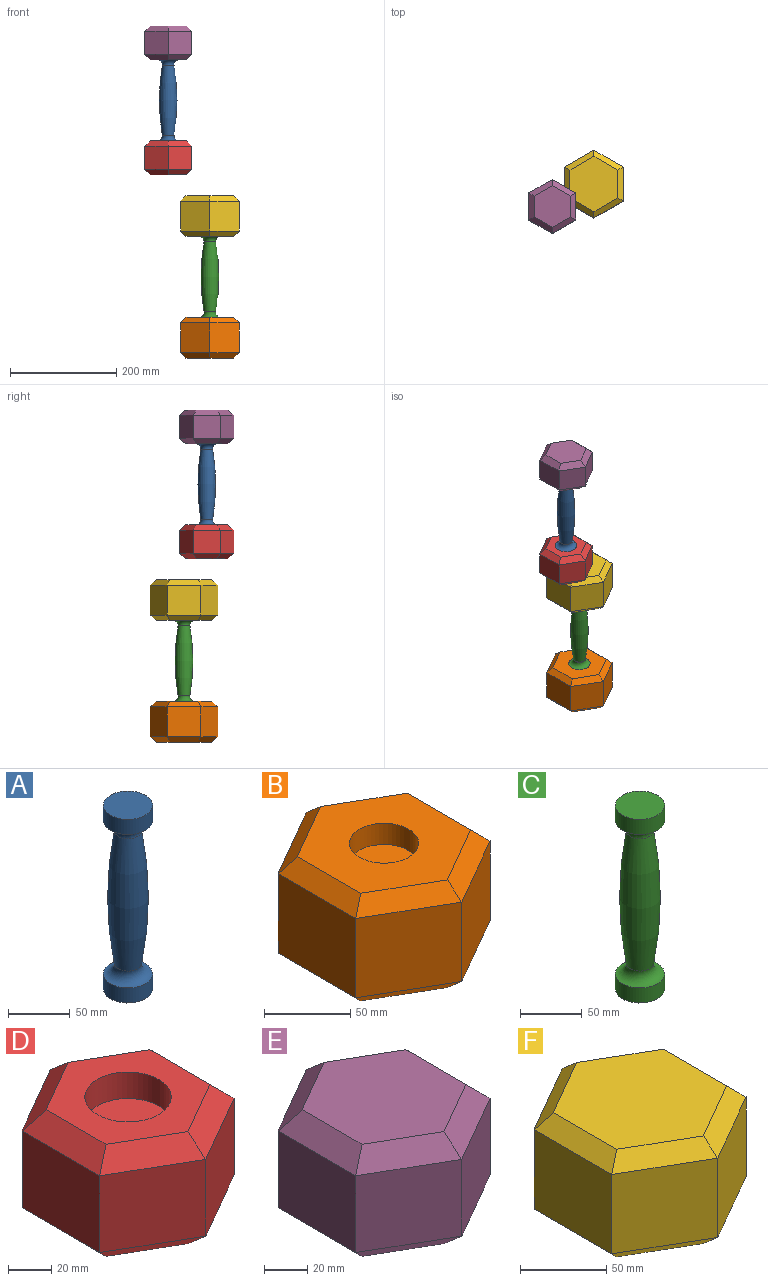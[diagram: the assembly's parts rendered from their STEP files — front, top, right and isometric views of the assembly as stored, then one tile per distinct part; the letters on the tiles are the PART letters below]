
ASSEMBLY  parts=6 mates=4
PART A: 7 faces, bbox 57.1x57.1x182.4 mm
  f0: plane 40x40mm, normal (0,0,1), area 1256.6mm2, adj f1
  f1: cylinder r=20mm len=40mm, axis (0,0,-1), area 1885mm2, adj f0,f2
  f2: torus R=20mm, axis (0,0,-1), area 1370.6mm2, adj f1,f3
  f3: revolved ~131.44x33.12mm, area 12232.8mm2, adj f2,f4
  f4: torus R=20mm, axis (0,0,-1), area 1370.6mm2, adj f3,f5
  f5: cylinder r=20mm len=40mm, axis (0,0,-1), area 1885mm2, adj f4,f6
  f6: plane 40x40mm, normal (0,0,-1), area 1256.6mm2, adj f5
PART B: 22 faces, bbox 110x127x76.2 mm
  f0: plane 103.91x89.99mm, normal (0,0,1), area 5755.9mm2, adj f3,f10,f11,f12,f13,f14,f15
  f1: plane 103.91x89.99mm, normal (0,0,-1), area 7012.5mm2, adj f16,f17,f18,f19,f20,f21
  f2: plane 40x40mm, normal (0,0,1), area 1256.6mm2, adj f3
  f3: cylinder r=20mm len=40mm, axis (0,0,-1), area 1885mm2, adj f0,f2
  f4: plane 63.5x56.2mm, normal (1,0,0), area 3568.7mm2, adj f7,f9,f11,f17
  f5: plane 56.2x54.99mm, normal (-0.5,0.87,0), area 3568.7mm2, adj f7,f8,f15,f18
  f6: plane 56.2x54.99mm, normal (-0.5,-0.87,0), area 3568.7mm2, adj f8,f9,f12,f21
  f7: plane 56.2x54.99mm, normal (0.5,0.87,0), area 3568.7mm2, adj f4,f5,f13,f16
  f8: plane 63.5x56.2mm, normal (-1,0,0), area 3568.7mm2, adj f5,f6,f14,f20
  f9: plane 56.2x54.99mm, normal (0.5,-0.87,0), area 3568.7mm2, adj f4,f6,f10,f19
  f10: plane 54.99x37.52mm, normal (0.35,-0.61,0.71), area 816.4mm2, adj f0,f9,f11,f12
  f11: plane 63.5x10mm, normal (0.71,0,0.71), area 816.4mm2, adj f0,f4,f10,f13
  f12: plane 54.99x37.52mm, normal (-0.35,-0.61,0.71), area 816.4mm2, adj f0,f6,f10,f14
  f13: plane 54.99x37.52mm, normal (0.35,0.61,0.71), area 816.4mm2, adj f0,f7,f11,f15
  f14: plane 63.5x10mm, normal (-0.71,0,0.71), area 816.4mm2, adj f0,f8,f12,f15
  f15: plane 54.99x37.52mm, normal (-0.35,0.61,0.71), area 816.4mm2, adj f0,f5,f13,f14
  f16: plane 54.99x37.52mm, normal (0.35,0.61,-0.71), area 816.4mm2, adj f1,f7,f17,f18
  f17: plane 63.5x10mm, normal (0.71,0,-0.71), area 816.4mm2, adj f1,f4,f16,f19
  f18: plane 54.99x37.52mm, normal (-0.35,0.61,-0.71), area 816.4mm2, adj f1,f5,f16,f20
  f19: plane 54.99x37.52mm, normal (0.35,-0.61,-0.71), area 816.4mm2, adj f1,f9,f17,f21
  f20: plane 63.5x10mm, normal (-0.71,0,-0.71), area 816.4mm2, adj f1,f8,f18,f21
  f21: plane 54.99x37.52mm, normal (-0.35,-0.61,-0.71), area 816.4mm2, adj f1,f6,f19,f20
PART C: 7 faces, bbox 57.1x57.1x182.4 mm
  f0: plane 40x40mm, normal (0,0,1), area 1256.6mm2, adj f1
  f1: cylinder r=20mm len=40mm, axis (0,0,-1), area 1885mm2, adj f0,f2
  f2: torus R=20mm, axis (0,0,-1), area 1370.6mm2, adj f1,f3
  f3: revolved ~131.44x33.12mm, area 12232.8mm2, adj f2,f4
  f4: torus R=20mm, axis (0,0,-1), area 1370.6mm2, adj f3,f5
  f5: cylinder r=20mm len=40mm, axis (0,0,-1), area 1885mm2, adj f4,f6
  f6: plane 40x40mm, normal (0,0,-1), area 1256.6mm2, adj f5
PART D: 22 faces, bbox 88x101.6x63.5 mm
  f0: plane 78.51x67.99mm, normal (0,0,1), area 2746.5mm2, adj f3,f10,f11,f12,f13,f14,f15
  f1: plane 78.51x67.99mm, normal (0,0,-1), area 4003.1mm2, adj f16,f17,f18,f19,f20,f21
  f2: plane 40x40mm, normal (0,0,1), area 1256.6mm2, adj f3
  f3: cylinder r=20mm len=40mm, axis (0,0,-1), area 1885mm2, adj f0,f2
  f4: plane 43.99x43.5mm, normal (0.5,0.87,0), area 2209.8mm2, adj f7,f9,f11,f17
  f5: plane 50.8x43.5mm, normal (-1,0,0), area 2209.8mm2, adj f7,f8,f15,f18
  f6: plane 43.99x43.5mm, normal (0.5,-0.87,0), area 2209.8mm2, adj f8,f9,f12,f21
  f7: plane 43.99x43.5mm, normal (-0.5,0.87,0), area 2209.8mm2, adj f4,f5,f13,f16
  f8: plane 43.99x43.5mm, normal (-0.5,-0.87,0), area 2209.8mm2, adj f5,f6,f14,f20
  f9: plane 50.8x43.5mm, normal (1,0,0), area 2209.8mm2, adj f4,f6,f10,f19
  f10: plane 50.8x10mm, normal (0.71,0,0.71), area 636.8mm2, adj f0,f9,f11,f12
  f11: plane 43.99x31.17mm, normal (0.35,0.61,0.71), area 636.8mm2, adj f0,f4,f10,f13
  f12: plane 43.99x31.17mm, normal (0.35,-0.61,0.71), area 636.8mm2, adj f0,f6,f10,f14
  f13: plane 43.99x31.17mm, normal (-0.35,0.61,0.71), area 636.8mm2, adj f0,f7,f11,f15
  f14: plane 43.99x31.17mm, normal (-0.35,-0.61,0.71), area 636.8mm2, adj f0,f8,f12,f15
  f15: plane 50.8x10mm, normal (-0.71,0,0.71), area 636.8mm2, adj f0,f5,f13,f14
  f16: plane 43.99x31.17mm, normal (-0.35,0.61,-0.71), area 636.8mm2, adj f1,f7,f17,f18
  f17: plane 43.99x31.17mm, normal (0.35,0.61,-0.71), area 636.8mm2, adj f1,f4,f16,f19
  f18: plane 50.8x10mm, normal (-0.71,0,-0.71), area 636.8mm2, adj f1,f5,f16,f20
  f19: plane 50.8x10mm, normal (0.71,0,-0.71), area 636.8mm2, adj f1,f9,f17,f21
  f20: plane 43.99x31.17mm, normal (-0.35,-0.61,-0.71), area 636.8mm2, adj f1,f8,f18,f21
  f21: plane 43.99x31.17mm, normal (0.35,-0.61,-0.71), area 636.8mm2, adj f1,f6,f19,f20
PART E: 22 faces, bbox 88x101.6x63.5 mm
  f0: plane 78.51x67.99mm, normal (0,0,-1), area 2746.5mm2, adj f1,f10,f11,f12,f13,f14,f15
  f1: cylinder r=20mm len=40mm, axis (0,0,-1), area 1885mm2, adj f0,f2
  f2: plane 40x40mm, normal (0,0,-1), area 1256.6mm2, adj f1
  f3: plane 78.51x67.99mm, normal (0,0,1), area 4003.1mm2, adj f16,f17,f18,f19,f20,f21
  f4: plane 43.99x43.5mm, normal (0.5,0.87,0), area 2209.8mm2, adj f7,f9,f14,f18
  f5: plane 50.8x43.5mm, normal (-1,0,0), area 2209.8mm2, adj f7,f8,f13,f17
  f6: plane 43.99x43.5mm, normal (0.5,-0.87,0), area 2209.8mm2, adj f8,f9,f10,f21
  f7: plane 43.99x43.5mm, normal (-0.5,0.87,0), area 2209.8mm2, adj f4,f5,f15,f16
  f8: plane 43.99x43.5mm, normal (-0.5,-0.87,0), area 2209.8mm2, adj f5,f6,f11,f19
  f9: plane 50.8x43.5mm, normal (1,0,0), area 2209.8mm2, adj f4,f6,f12,f20
  f10: plane 43.99x31.17mm, normal (0.35,-0.61,-0.71), area 636.8mm2, adj f0,f6,f11,f12
  f11: plane 43.99x31.17mm, normal (-0.35,-0.61,-0.71), area 636.8mm2, adj f0,f8,f10,f13
  f12: plane 50.8x10mm, normal (0.71,0,-0.71), area 636.8mm2, adj f0,f9,f10,f14
  f13: plane 50.8x10mm, normal (-0.71,0,-0.71), area 636.8mm2, adj f0,f5,f11,f15
  f14: plane 43.99x31.17mm, normal (0.35,0.61,-0.71), area 636.8mm2, adj f0,f4,f12,f15
  f15: plane 43.99x31.17mm, normal (-0.35,0.61,-0.71), area 636.8mm2, adj f0,f7,f13,f14
  f16: plane 43.99x31.17mm, normal (-0.35,0.61,0.71), area 636.8mm2, adj f3,f7,f17,f18
  f17: plane 50.8x10mm, normal (-0.71,0,0.71), area 636.8mm2, adj f3,f5,f16,f19
  f18: plane 43.99x31.17mm, normal (0.35,0.61,0.71), area 636.8mm2, adj f3,f4,f16,f20
  f19: plane 43.99x31.17mm, normal (-0.35,-0.61,0.71), area 636.8mm2, adj f3,f8,f17,f21
  f20: plane 50.8x10mm, normal (0.71,0,0.71), area 636.8mm2, adj f3,f9,f18,f21
  f21: plane 43.99x31.17mm, normal (0.35,-0.61,0.71), area 636.8mm2, adj f3,f6,f19,f20
PART F: 22 faces, bbox 110x127x76.2 mm
  f0: plane 103.91x89.99mm, normal (0,0,-1), area 5755.9mm2, adj f1,f10,f11,f12,f13,f14,f15
  f1: cylinder r=20mm len=40mm, axis (0,0,-1), area 1885mm2, adj f0,f2
  f2: plane 40x40mm, normal (0,0,-1), area 1256.6mm2, adj f1
  f3: plane 103.91x89.99mm, normal (0,0,1), area 7012.5mm2, adj f16,f17,f18,f19,f20,f21
  f4: plane 63.5x56.2mm, normal (1,0,0), area 3568.7mm2, adj f7,f9,f15,f18
  f5: plane 56.2x54.99mm, normal (-0.5,0.87,0), area 3568.7mm2, adj f7,f8,f11,f17
  f6: plane 56.2x54.99mm, normal (-0.5,-0.87,0), area 3568.7mm2, adj f8,f9,f12,f21
  f7: plane 56.2x54.99mm, normal (0.5,0.87,0), area 3568.7mm2, adj f4,f5,f13,f16
  f8: plane 63.5x56.2mm, normal (-1,0,0), area 3568.7mm2, adj f5,f6,f10,f19
  f9: plane 56.2x54.99mm, normal (0.5,-0.87,0), area 3568.7mm2, adj f4,f6,f14,f20
  f10: plane 63.5x10mm, normal (-0.71,0,-0.71), area 816.4mm2, adj f0,f8,f11,f12
  f11: plane 54.99x37.52mm, normal (-0.35,0.61,-0.71), area 816.4mm2, adj f0,f5,f10,f13
  f12: plane 54.99x37.52mm, normal (-0.35,-0.61,-0.71), area 816.4mm2, adj f0,f6,f10,f14
  f13: plane 54.99x37.52mm, normal (0.35,0.61,-0.71), area 816.4mm2, adj f0,f7,f11,f15
  f14: plane 54.99x37.52mm, normal (0.35,-0.61,-0.71), area 816.4mm2, adj f0,f9,f12,f15
  f15: plane 63.5x10mm, normal (0.71,0,-0.71), area 816.4mm2, adj f0,f4,f13,f14
  f16: plane 54.99x37.52mm, normal (0.35,0.61,0.71), area 816.4mm2, adj f3,f7,f17,f18
  f17: plane 54.99x37.52mm, normal (-0.35,0.61,0.71), area 816.4mm2, adj f3,f5,f16,f19
  f18: plane 63.5x10mm, normal (0.71,0,0.71), area 816.4mm2, adj f3,f4,f16,f20
  f19: plane 63.5x10mm, normal (-0.71,0,0.71), area 816.4mm2, adj f3,f8,f17,f21
  f20: plane 54.99x37.52mm, normal (0.35,-0.61,0.71), area 816.4mm2, adj f3,f9,f18,f21
  f21: plane 54.99x37.52mm, normal (-0.35,-0.61,0.71), area 816.4mm2, adj f3,f6,f19,f20
PLACE A t=(-78.4,-42.77,14.38)mm
PLACE B at identity
PLACE C at identity
PLACE D t=(-78.4,-42.77,14.38)mm
PLACE E t=(-78.4,-42.77,14.38)mm
PLACE F at identity
MATE fastened D.f3 <-> A.f1  axis (0,0,1) through (-78.4,-42.77,1663.08)mm
MATE fastened F.f1 <-> C.f1  axis (0,0,-1) through (0,0,1513.6)mm
MATE fastened C.f1 <-> B.f3  axis (0,0,-1) through (0,0,1331.2)mm
MATE fastened A.f1 <-> E.f1  axis (0,0,1) through (-78.4,-42.77,1845.48)mm
